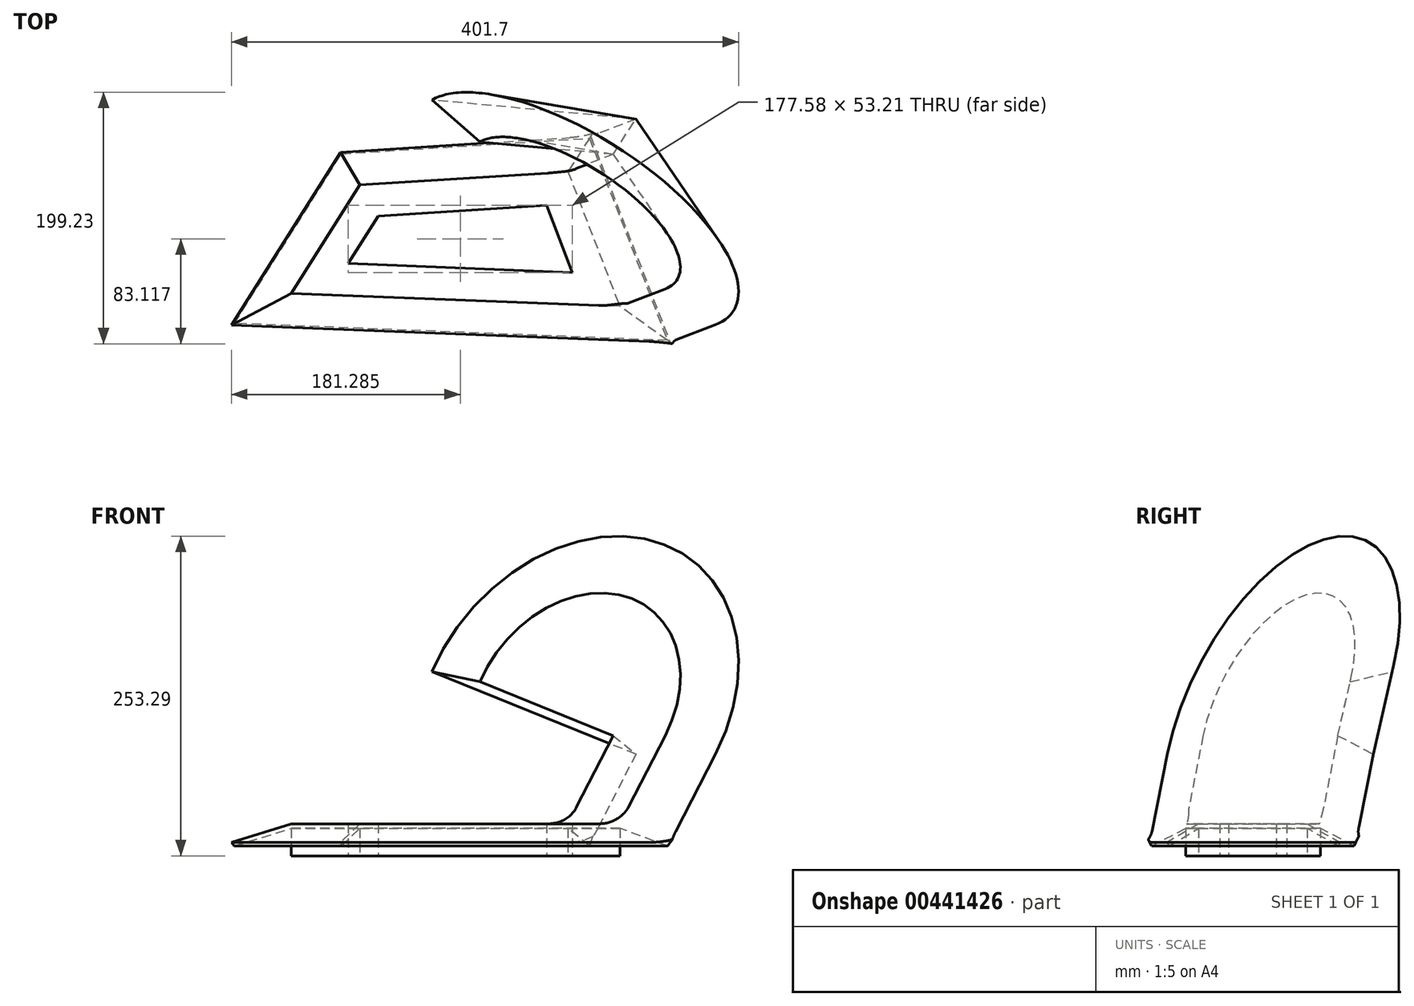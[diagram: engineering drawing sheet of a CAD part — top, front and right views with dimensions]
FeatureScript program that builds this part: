
annotation { "Feature Type Name" : "Feature", "Feature Type Description" : "" }
export const myFeature = defineFeature(function(context is Context, id is Id, definition is map)
    precondition{}
    {
        {
            var Q0;
            Q0=qCreatedBy(makeId("Top.planeOp"),FACE);
            var sketch = newSketch(context, id + "F0", { "sketchPlane" : qUnion([Q0])});
            skLineSegment(sketch, "E0", {"start": v(-155.9, -4.43) * mm, "end": v(-101.65, 81.48) * mm});
            skLineSegment(sketch, "E1", {"start": v(-101.65, 81.48) * mm, "end": v(63.12, 91.9) * mm});
            skLineSegment(sketch, "E2", {"start": v(63.12, 91.9) * mm, "end": v(104.25, -14.74) * mm});
            skLineSegment(sketch, "E3", {"start": v(104.25, -14.74) * mm, "end": v(-155.9, -4.43) * mm});
            skLineSegment(sketch, "E4.0", {"start": v(-87.1, 56.95) * mm, "end": v(46.12, 65.38) * mm});
            skLineSegment(sketch, "E4.1", {"start": v(-110.93, 19.21) * mm, "end": v(-87.1, 56.95) * mm});
            skLineSegment(sketch, "E4.2", {"start": v(66.64, 12.17) * mm, "end": v(-110.93, 19.21) * mm});
            skLineSegment(sketch, "E4.3", {"start": v(46.12, 65.38) * mm, "end": v(66.64, 12.17) * mm});
            skSolve(sketch);
        }
        {
            var Q0;
            Q0=makeQuery(id+"F0.imprint","IMPRINT",FACE,{"disambiguationData":[TD([[makeQuery(id+"F0.imprint","IMPRINT",EDGE,{"derivedFrom":sQuery(id+"F0.wireOp",EDGE,"E0")}),-1.0]])]});
            extrude(context, id + "F1", {"entities" : qUnion([Q0]), "depth" : 25.4 * mm});
        }
        {
            var Q0;
            Q0=makeQuery(id+"F1.opExtrude","SWEPT_FACE",FACE,{"disambiguationData":[OSD([sQuery(id+"F0.wireOp",EDGE,"E2")])]});
            var sketch = newSketch(context, id + "F2", { "sketchPlane" : qUnion([Q0])});
            skLineSegment(sketch, "E5", {"start": v(-51.26, 25.4) * mm, "end": v(-80.5, 10.63) * mm});
            skLineSegment(sketch, "E6", {"start": v(-80.5, 10.63) * mm, "end": v(-79.05, 7.75) * mm});
            skLineSegment(sketch, "E7", {"start": v(-79.05, 7.75) * mm, "end": v(-51.26, 21.78) * mm});
            skSolve(sketch);
        }
        {
            var Q0;
            {var subQ0=sQuery(id+"F2.wireOp",EDGE,"E5");Q0=makeQuery(id+"F2.imprint","IMPRINT",FACE,{"disambiguationData":[TD([[makeQuery(id+"F2.imprint","IMPRINT",EDGE,{"derivedFrom":subQ0}),1.0]])]});}
            var Q1;
            Q1=makeQuery(id+"F1.opExtrude","CAP_EDGE",EDGE,{"disambiguationData":[OSD([sQuery(id+"F0.wireOp",EDGE,"E3")])],"isStart":false});
            var Q2;
            Q2=makeQuery(id+"F1.opExtrude","CAP_EDGE",EDGE,{"disambiguationData":[OSD([sQuery(id+"F0.wireOp",EDGE,"E0")])],"isStart":false});
            var Q3;
            Q3=makeQuery(id+"F1.opExtrude","CAP_EDGE",EDGE,{"disambiguationData":[OSD([sQuery(id+"F0.wireOp",EDGE,"E1")])],"isStart":false});
            var Q4;
            Q4=makeQuery(id+"F1.opExtrude","CAP_EDGE",EDGE,{"disambiguationData":[OSD([sQuery(id+"F0.wireOp",EDGE,"E2")])],"isStart":false});
            sweep(context, id + "F3", {"operationType" : NewBodyOperationType.ADD, "profiles" : qUnion([Q0]), "path" : qUnion([Q1, Q2, Q3, Q4])});
        }
        {
            var Q0;
            Q0=makeQuery(id+"F3.opSweep","SWEPT_FACE",FACE,{"disambiguationData":[OSD([sQuery(id+"F0.wireOp",EDGE,"E2"),sQuery(id+"F2.wireOp",EDGE,"E5")])]});
            extrude(context, id + "F4", {"entities" : qUnion([Q0]), "operationType" : NewBodyOperationType.ADD, "depth" : 79.76 * mm, "offsetDistance" : 25.4 * mm});
        }
        {
            var Q0;
            {var subQ0=sQuery(id+"F2.wireOp",EDGE,"E5");var subQ1=sQuery(id+"F0.wireOp",EDGE,"E3");var subQ2=sQuery(id+"F0.wireOp",EDGE,"E2");var subQ3=makeQuery(id+"F3.opSweep","CAP_EDGE",EDGE,{"disambiguationData":[OSD([subQ2,subQ1,subQ0])],"isStart":true});Q0=makeQuery(id+"F4.boolean.opBoolean","MERGE",EDGE,{"derivedFrom":[subQ3,makeQuery(id+"F4.opExtrude","CAP_EDGE",EDGE,{"disambiguationData":[OSD([subQ2,subQ1,subQ0]),TDD([subQ3])],"isStart":true})]});}
            var Q1;
            {var subQ0=sQuery(id+"F2.wireOp",EDGE,"E5");var subQ1=sQuery(id+"F0.wireOp",EDGE,"E2");var subQ2=makeQuery(id+"F1.opExtrude","CAP_EDGE",EDGE,{"disambiguationData":[OSD([subQ1])],"isStart":false});var subQ3=sQuery(id+"F0.wireOp",EDGE,"E3");var subQ4=makeQuery(id+"F3.boolean.opBoolean","MERGE",EDGE,{"derivedFrom":[subQ2,makeQuery(id+"F3.opSweep","SWEPT_EDGE",EDGE,{"disambiguationData":[OSD([subQ1,subQ3,subQ0]),TDD([subQ2,makeQuery(id+"F2.imprint","INTERSECT",VERTEX,{"derivedFrom":[makeQuery(id+"F1.opExtrude","SWEPT_EDGE",EDGE,{"disambiguationData":[OSD([subQ1,subQ3])]}),subQ2,subQ0]})])]})]});Q1=makeQuery(id+"F4.boolean.opBoolean","MERGE",EDGE,{"derivedFrom":[subQ4,makeQuery(id+"F4.opExtrude","CAP_EDGE",EDGE,{"disambiguationData":[OSD([subQ1,subQ3,subQ0]),TDD([subQ4])],"isStart":true})]});}
            var Q2;
            {var subQ0=sQuery(id+"F2.wireOp",EDGE,"E5");var subQ1=sQuery(id+"F0.wireOp",EDGE,"E2");var subQ2=sQuery(id+"F0.wireOp",EDGE,"E1");Q2=makeQuery(id+"F4.boolean.opBoolean","MERGE",EDGE,{"derivedFrom":[makeQuery(id+"F3.opSweep","MID_CAP_EDGE",EDGE,{"disambiguationData":[OSD([subQ2,subQ1,subQ0])],"capPos":3.0}),makeQuery(id+"F4.opExtrude","CAP_EDGE",EDGE,{"disambiguationData":[OSD([subQ2,subQ1,subQ0])],"isStart":true})]});}
            fillet(context, id + "F5", {"entities" : qUnion([Q0, Q1, Q2]), "tangentPropagation" : true, "radius" : 25.4 * mm, "defaultsChanged" : true, "vertexSettings" : [], "allowEdgeOverflow" : false});
        }
        {
            var Q0;
            Q0=makeQuery(id+"F4.opExtrude","CAP_FACE",FACE,{"disambiguationData":[OSD([sQuery(id+"F0.wireOp",EDGE,"E2"),sQuery(id+"F2.wireOp",EDGE,"E5")])],"isStart":false});
            var Q1;
            Q1=makeQuery(id+"F4.opExtrude","CAP_EDGE",EDGE,{"disambiguationData":[OSD([sQuery(id+"F0.wireOp",EDGE,"E1"),sQuery(id+"F0.wireOp",EDGE,"E2"),sQuery(id+"F2.wireOp",EDGE,"E5")])],"isStart":false});
            revolve(context, id + "F6", {"operationType" : NewBodyOperationType.ADD, "surfaceOperationType" : NewSurfaceOperationType.NEW, "entities" : qUnion([Q0]), "axis" : qUnion([Q1]), "revolveType" : RevolveType.ONE_DIRECTION, "oppositeDirection" : true, "angle" : 185 * degree});
        }
    });
